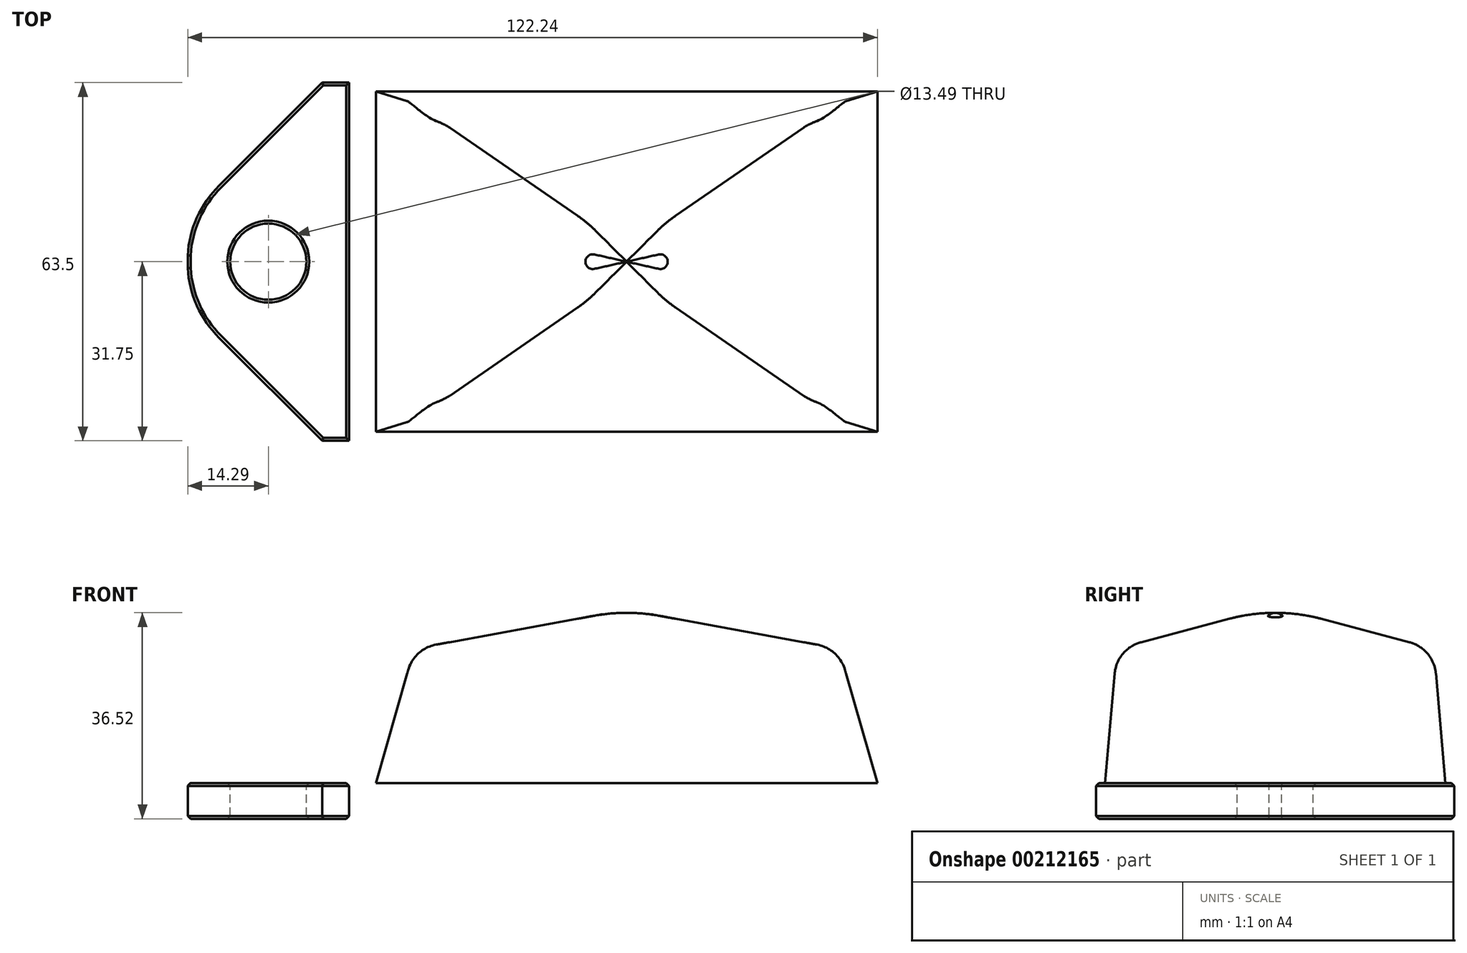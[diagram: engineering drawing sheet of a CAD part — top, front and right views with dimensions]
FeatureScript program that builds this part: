
annotation { "Feature Type Name" : "Feature", "Feature Type Description" : "" }
export const myFeature = defineFeature(function(context is Context, id is Id, definition is map)
    precondition{}
    {
        {
            var Q0;
            Q0=qCreatedBy(makeId("Right.planeOp"),FACE);
            var sketch = newSketch(context, id + "F0", { "sketchPlane" : qUnion([Q0])});
            skLineSegment(sketch, "E0.bottom", {"start": v(-31.75, 3.17) * mm, "end": v(31.75, 3.17) * mm});
            skLineSegment(sketch, "E0.top", {"start": v(-31.75, -3.17) * mm, "end": v(31.75, -3.17) * mm});
            skLineSegment(sketch, "E0.left", {"start": v(-31.75, 3.17) * mm, "end": v(-31.75, -3.17) * mm});
            skLineSegment(sketch, "E0.right", {"start": v(31.75, 3.17) * mm, "end": v(31.75, -3.17) * mm});
            skPoint(sketch, "E0.middle", {"position": v(0, 0) * mm});
            skLineSegment(sketch, "E1", {"start": v(0, 3.17) * mm, "end": v(0, 33.34) * mm, "construction": true});
            skPoint(sketch, "E1.endSnap0", {"position": v(0, 3.17) * mm});
            skLineSegment(sketch, "E2", {"start": v(0, 0) * mm, "end": v(30.16, 0) * mm, "construction": true});
            skLineSegment(sketch, "E3", {"start": v(0, 0) * mm, "end": v(-30.16, 0) * mm, "construction": true});
            skLineSegment(sketch, "E4", {"start": v(30.16, 0) * mm, "end": v(30.16, 3.17) * mm, "construction": true});
            skLineSegment(sketch, "E5", {"start": v(-30.16, 0) * mm, "end": v(-30.16, 3.17) * mm, "construction": true});
            skLineSegment(sketch, "E6", {"start": v(0, 26.99) * mm, "end": v(-32.25, 26.99) * mm, "construction": true});
            skLineSegment(sketch, "E7", {"start": v(30.16, 3.17) * mm, "end": v(28.47, 22.55) * mm});
            skLineSegment(sketch, "E8", {"start": v(0, 26.99) * mm, "end": v(37.6, 26.99) * mm, "construction": true});
            skPoint(sketch, "E9.visualSharp", {"position": v(0, 33.34) * mm});
            skPoint(sketch, "E10", {"position": v(0, 1.59) * mm});
            skLineSegment(sketch, "E11", {"start": v(23.77, 28.13) * mm, "end": v(8.14, 32.28) * mm});
            skPoint(sketch, "E12.visualSharp", {"position": v(28.08, 26.99) * mm});
            skLineSegment(sketch, "E13.MirrorCS", {"start": v(-23.77, 28.13) * mm, "end": v(-8.14, 32.28) * mm});
            skLineSegment(sketch, "E14.MirrorCS", {"start": v(-30.16, 3.17) * mm, "end": v(-28.47, 22.55) * mm});
            skArc(sketch, "E15", {"start": v(8.14, 32.28) * mm, "mid": v(0, 33.34) * mm, "end": v(-8.14, 32.28) * mm});
            skLineSegment(sketch, "E16", {"start": v(30.16, 3.17) * mm, "end": v(67.45, 3.17) * mm});
            skLineSegment(sketch, "E17", {"start": v(67.45, 3.17) * mm, "end": v(67.45, 46.58) * mm});
            skLineSegment(sketch, "E18", {"start": v(67.45, 46.58) * mm, "end": v(-44.32, 46.58) * mm});
            skLineSegment(sketch, "E19", {"start": v(-44.32, 46.58) * mm, "end": v(-44.32, 3.17) * mm});
            skLineSegment(sketch, "E20", {"start": v(-44.32, 3.17) * mm, "end": v(-31.75, 3.17) * mm});
            skLineSegment(sketch, "E21", {"start": v(-44.32, 3.17) * mm, "end": v(-44.32, -48.14) * mm});
            skLineSegment(sketch, "E22", {"start": v(-44.32, -48.14) * mm, "end": v(67.45, -48.14) * mm});
            skLineSegment(sketch, "E23", {"start": v(67.45, -48.14) * mm, "end": v(67.45, 3.17) * mm});
            skLineSegment(sketch, "E24", {"start": v(23.77, 28.13) * mm, "end": v(28.08, 26.99) * mm});
            skLineSegment(sketch, "E25", {"start": v(28.47, 22.55) * mm, "end": v(28.08, 26.99) * mm});
            skLineSegment(sketch, "E26.MirrorCS", {"start": v(-23.77, 28.13) * mm, "end": v(-28.08, 26.99) * mm});
            skLineSegment(sketch, "E27.MirrorCS", {"start": v(-28.47, 22.55) * mm, "end": v(-28.08, 26.99) * mm});
            skSolve(sketch);
        }
        {
            var Q0;
            Q0=makeQuery(id+"F0.imprint","IMPRINT",FACE,{"disambiguationData":[TD([[makeQuery(id+"F0.imprint","IMPRINT",EDGE,{"derivedFrom":sQuery(id+"F0.wireOp",EDGE,"E0.top")}),1.0]])]});
            extrude(context, id + "F1", {"entities" : qUnion([Q0]), "endBound" : BoundingType.SYMMETRIC, "depth" : 155.57 * mm});
        }
        {
            var Q0;
            Q0=qCreatedBy(makeId("Right.planeOp"),FACE);
            var sketch = newSketch(context, id + "F2", { "sketchPlane" : qUnion([Q0])});
            skLineSegment(sketch, "E28", {"start": v(0, 0) * mm, "end": v(0, 33.34) * mm, "construction": true});
            skLineSegment(sketch, "E29", {"start": v(0, 33.34) * mm, "end": v(0, -33.34) * mm});
            skArc(sketch, "E30", {"start": v(0, -33.34) * mm, "mid": v(33.34, 0) * mm, "end": v(0, 33.34) * mm});
            skSolve(sketch);
        }
        {
            var Q0;
            Q0=qCreatedBy(makeId("Front.planeOp"),FACE);
            var sketch = newSketch(context, id + "F3", { "sketchPlane" : qUnion([Q0])});
            skLineSegment(sketch, "E31", {"start": v(0, 0) * mm, "end": v(0, 33.34) * mm, "construction": true});
            skLineSegment(sketch, "E32", {"start": v(0, 3.18) * mm, "end": v(-44.45, 3.17) * mm, "construction": true});
            skLineSegment(sketch, "E33", {"start": v(-44.45, 3.17) * mm, "end": v(-38.7, 23.2) * mm});
            skLineSegment(sketch, "E34", {"start": v(-44.45, 3.17) * mm, "end": v(-44.45, 26.99) * mm});
            skLineSegment(sketch, "E35", {"start": v(-44.45, 26.99) * mm, "end": v(-37.62, 26.99) * mm, "construction": true});
            skLineSegment(sketch, "E36", {"start": v(0, 33.34) * mm, "end": v(-44.45, 33.34) * mm});
            skLineSegment(sketch, "E37", {"start": v(-44.45, 33.34) * mm, "end": v(-44.45, 26.99) * mm});
            skLineSegment(sketch, "E38.MirrorCS", {"start": v(44.45, 3.17) * mm, "end": v(38.96, 22.33) * mm});
            skLineSegment(sketch, "E39.MirrorCS", {"start": v(44.45, 3.17) * mm, "end": v(44.45, 26.99) * mm});
            skLineSegment(sketch, "E40.MirrorCS", {"start": v(44.45, 33.34) * mm, "end": v(44.45, 26.99) * mm});
            skLineSegment(sketch, "E41.MirrorCS", {"start": v(0, 33.34) * mm, "end": v(44.45, 33.34) * mm});
            skPoint(sketch, "E42.visualSharp", {"position": v(0, 33.34) * mm});
            skPoint(sketch, "E43", {"position": v(0, 1.59) * mm});
            skLineSegment(sketch, "E44", {"start": v(0, 1.59) * mm, "end": v(31.18, 32.77) * mm, "construction": true});
            skLineSegment(sketch, "E45.MirrorCS", {"start": v(0, 1.59) * mm, "end": v(-31.18, 32.77) * mm, "construction": true});
            skLineSegment(sketch, "E46.0", {"start": v(15.88, 0) * mm, "end": v(15.88, 30.3) * mm, "construction": true});
            skLineSegment(sketch, "E47.0", {"start": v(-15.88, 0) * mm, "end": v(-15.88, 30.3) * mm, "construction": true});
            skPoint(sketch, "E48.orphan", {"position": v(-38.96, 22.33) * mm});
            skLineSegment(sketch, "E49", {"start": v(-33.75, 27.7) * mm, "end": v(-5.7, 32.82) * mm});
            skLineSegment(sketch, "E50.MirrorCS", {"start": v(44.45, 3.17) * mm, "end": v(38.7, 23.2) * mm});
            skLineSegment(sketch, "E51.MirrorCS", {"start": v(33.75, 27.7) * mm, "end": v(5.7, 32.82) * mm});
            skPoint(sketch, "E52.visualSharp", {"position": v(-37.62, 26.99) * mm});
            skPoint(sketch, "E53.visualSharp", {"position": v(37.62, 26.99) * mm});
            skArc(sketch, "E54", {"start": v(5.7, 32.82) * mm, "mid": v(0, 33.34) * mm, "end": v(-5.7, 32.82) * mm});
            skLineSegment(sketch, "E55", {"start": v(44.45, 3.17) * mm, "end": v(-44.45, 3.17) * mm});
            skLineSegment(sketch, "E56", {"start": v(38.7, 23.2) * mm, "end": v(37.62, 26.99) * mm});
            skLineSegment(sketch, "E57", {"start": v(33.75, 27.7) * mm, "end": v(37.62, 26.99) * mm});
            skLineSegment(sketch, "E58", {"start": v(-33.75, 27.7) * mm, "end": v(-37.62, 26.99) * mm});
            skLineSegment(sketch, "E59", {"start": v(-38.7, 23.2) * mm, "end": v(-37.62, 26.99) * mm});
            skSolve(sketch);
        }
        {
            var Q0;
            Q0=qCreatedBy(makeId("Top.planeOp"),FACE);
            var sketch = newSketch(context, id + "F4", { "sketchPlane" : qUnion([Q0])});
            skLineSegment(sketch, "E60", {"start": v(0, 0) * mm, "end": v(-63.5, 0) * mm, "construction": true});
            skLineSegment(sketch, "E61.MirrorCS", {"start": v(0, 0) * mm, "end": v(63.5, 0) * mm, "construction": true});
            skCircle(sketch, "E62", {"center": v(-63.5, 0) * mm, "radius": 6.75 * mm});
            skCircle(sketch, "E63.MirrorC", {"center": v(63.5, 0) * mm, "radius": 6.75 * mm});
            skLineSegment(sketch, "E64", {"start": v(0, 0) * mm, "end": v(-85.72, 0) * mm, "construction": true});
            skLineSegment(sketch, "E65", {"start": v(-72.23, -13.5) * mm, "end": v(-53.98, -31.75) * mm});
            skLineSegment(sketch, "E66.MirrorCS", {"start": v(-72.23, 13.5) * mm, "end": v(-53.98, 31.75) * mm});
            skLineSegment(sketch, "E67", {"start": v(0, 0) * mm, "end": v(0, -31.75) * mm, "construction": true});
            skLineSegment(sketch, "E68", {"start": v(0, -31.75) * mm, "end": v(-53.98, -31.75) * mm});
            skPoint(sketch, "E69.orphan", {"position": v(-45.67, -40.06) * mm});
            skLineSegment(sketch, "E70.MirrorCS", {"start": v(0, 31.75) * mm, "end": v(-53.98, 31.75) * mm});
            skLineSegment(sketch, "E71.MirrorCS", {"start": v(0, 0) * mm, "end": v(0, 31.75) * mm, "construction": true});
            skPoint(sketch, "E72.orphan", {"position": v(-45.67, 40.06) * mm});
            skPoint(sketch, "E73", {"position": v(-58.74, 0) * mm});
            skLineSegment(sketch, "E74", {"start": v(-58.74, 0) * mm, "end": v(-72.23, 13.5) * mm, "construction": true});
            skLineSegment(sketch, "E75.MirrorCS", {"start": v(-58.74, 0) * mm, "end": v(-72.23, -13.5) * mm, "construction": true});
            skLineSegment(sketch, "E76", {"start": v(-85.72, 0) * mm, "end": v(-85.72, -31.75) * mm});
            skLineSegment(sketch, "E77", {"start": v(-85.72, -31.75) * mm, "end": v(-53.98, -31.75) * mm});
            skLineSegment(sketch, "E78", {"start": v(-85.73, 0) * mm, "end": v(-85.73, 31.75) * mm});
            skLineSegment(sketch, "E79", {"start": v(-85.73, 31.75) * mm, "end": v(-53.98, 31.75) * mm});
            skArc(sketch, "E80.MirrorCS", {"start": v(72.23, 13.5) * mm, "mid": v(77.82, 0) * mm, "end": v(72.23, -13.5) * mm});
            skLineSegment(sketch, "E81.MirrorCS", {"start": v(85.73, 0) * mm, "end": v(53.98, 31.75) * mm});
            skLineSegment(sketch, "E82.MirrorCS", {"start": v(85.73, 31.75) * mm, "end": v(53.98, 31.75) * mm});
            skLineSegment(sketch, "E83.MirrorCS", {"start": v(85.73, 0) * mm, "end": v(85.73, 31.75) * mm});
            skLineSegment(sketch, "E84.MirrorCS", {"start": v(85.72, 0) * mm, "end": v(85.72, -31.75) * mm});
            skLineSegment(sketch, "E85.MirrorCS", {"start": v(85.72, -31.75) * mm, "end": v(53.98, -31.75) * mm});
            skLineSegment(sketch, "E86.MirrorCS", {"start": v(85.73, 0) * mm, "end": v(53.98, -31.75) * mm});
            skArc(sketch, "E87", {"start": v(-72.23, -13.5) * mm, "mid": v(-77.82, 0) * mm, "end": v(-72.23, 13.5) * mm});
            skPoint(sketch, "E88.orphan", {"position": v(-85.73, 0) * mm});
            skSolve(sketch);
        }
        {
            var Q0;
            Q0=makeQuery(id+"F3.imprint","IMPRINT",FACE,{"disambiguationData":[TD([[makeQuery(id+"F3.imprint","IMPRINT",EDGE,{"derivedFrom":sQuery(id+"F3.wireOp",EDGE,"E33")}),-1.0]])]});
            extrude(context, id + "F5", {"entities" : qUnion([Q0]), "endBound" : BoundingType.SYMMETRIC, "depth" : 60.32 * mm});
        }
        {
            var Q0;
            {var subQ0=sQuery(id+"F0.wireOp",EDGE,"E7");Q0=makeQuery(id+"F0.imprint","IMPRINT",FACE,{"disambiguationData":[TD([[makeQuery(id+"F0.imprint","IMPRINT",EDGE,{"derivedFrom":subQ0}),1.0]])]});}
            extrude(context, id + "F6", {"entities" : qUnion([Q0]), "operationType" : NewBodyOperationType.ADD, "endBound" : BoundingType.SYMMETRIC, "depth" : 88.9 * mm});
        }
        {
            var Q0;
            {var subQ1=sQuery(id+"F3.wireOp",EDGE,"E39.MirrorCS");Q0=makeQuery(id+"F3.imprint","IMPRINT",FACE,{"disambiguationData":[TD([[makeQuery(id+"F3.imprint","IMPRINT",EDGE,{"derivedFrom":subQ1}),1.0]])]});}
            var Q1;
            Q1=makeQuery(id+"F3.imprint","IMPRINT",FACE,{"disambiguationData":[TD([[makeQuery(id+"F3.imprint","IMPRINT",EDGE,{"derivedFrom":sQuery(id+"F3.wireOp",EDGE,"E33")}),1.0]])]});
            extrude(context, id + "F7", {"entities" : qUnion([Q0, Q1]), "operationType" : NewBodyOperationType.REMOVE, "endBound" : BoundingType.SYMMETRIC, "oppositeDirection" : true, "depth" : 60.32 * mm});
        }
        {
            var Q0;
            {var subQ4=sQuery(id+"F0.wireOp",EDGE,"E7");Q0=makeQuery(id+"F0.imprint","IMPRINT",FACE,{"disambiguationData":[TD([[makeQuery(id+"F0.imprint","IMPRINT",EDGE,{"derivedFrom":subQ4}),-1.0]])]});}
            extrude(context, id + "F8", {"entities" : qUnion([Q0]), "operationType" : NewBodyOperationType.REMOVE, "endBound" : BoundingType.SYMMETRIC, "oppositeDirection" : true, "depth" : 88.9 * mm});
        }
        {
            var Q0;
            Q0=makeQuery(id+"F2.imprint","IMPRINT",FACE,{"disambiguationData":[TD([[makeQuery(id+"F2.imprint","IMPRINT",EDGE,{"derivedFrom":sQuery(id+"F2.wireOp",EDGE,"E29")}),1.0]])]});
            var Q1;
            Q1=sQuery(id+"F2.wireOp",EDGE,"E30");
            var Q2;
            Q2=sQuery(id+"F2.wireOp",EDGE,"E29");
            revolve(context, id + "F9", {"operationType" : NewBodyOperationType.ADD, "entities" : qUnion([Q0]), "surfaceEntities" : qUnion([Q1]), "axis" : qUnion([Q2]), "revolveType" : RevolveType.FULL});
        }
        {
            var Q0;
            Q0=makeQuery(id+"F1.opExtrude","CAP_FACE",FACE,{"disambiguationData":[OSD([sQuery(id+"F0.wireOp",EDGE,"E0.bottom"),sQuery(id+"F0.wireOp",EDGE,"E0.top"),sQuery(id+"F0.wireOp",EDGE,"E0.left"),sQuery(id+"F0.wireOp",EDGE,"E0.right"),sQuery(id+"F0.wireOp",EDGE,"E16")])],"isStart":false});
            var Q1;
            {var subQ4=sQuery(id+"F0.wireOp",EDGE,"E7");Q1=makeQuery(id+"F0.imprint","IMPRINT",FACE,{"disambiguationData":[TD([[makeQuery(id+"F0.imprint","IMPRINT",EDGE,{"derivedFrom":subQ4}),-1.0]])]});}
            var Q2;
            Q2=makeQuery(id+"F0.imprint","IMPRINT",FACE,{"disambiguationData":[TD([[makeQuery(id+"F0.imprint","IMPRINT",EDGE,{"derivedFrom":sQuery(id+"F0.wireOp",EDGE,"E0.top")}),-1.0]])]});
            extrude(context, id + "F10", {"entities" : qUnion([Q0, Q1, Q2]), "operationType" : NewBodyOperationType.REMOVE, "endBound" : BoundingType.SYMMETRIC, "oppositeDirection" : true, "depth" : 254 * mm});
        }
        {
            var Q0;
            Q0=makeQuery(id+"F8.boolean.opBoolean","COPY",EDGE,{"derivedFrom":makeQuery(id+"F8.opExtrude","SWEPT_EDGE",EDGE,{"disambiguationData":[OSD([sQuery(id+"F0.wireOp",EDGE,"E26.MirrorCS"),sQuery(id+"F0.wireOp",EDGE,"E27.MirrorCS")])]})});
            var Q1;
            {var subQ0=sQuery(id+"F3.wireOp",EDGE,"E57");var subQ1=sQuery(id+"F3.wireOp",EDGE,"E56");var subQ12=makeQuery(id+"F5.opExtrude","SWEPT_EDGE",EDGE,{"disambiguationData":[OSD([subQ1,subQ0])]});Q1=makeQuery(id+"F7.boolean.opBoolean","MERGE",EDGE,{"derivedFrom":[makeQuery(id+"F6.boolean.opBoolean","SPLIT",EDGE,{"disambiguationData":[TD([makeQuery(id+"F6.opExtrude","SWEPT_FACE",FACE,{"disambiguationData":[OSD([sQuery(id+"F0.wireOp",EDGE,"E7"),sQuery(id+"F0.wireOp",EDGE,"E25")])]})])],"derivedFrom":subQ12}),makeQuery(id+"F6.boolean.opBoolean","SPLIT",EDGE,{"disambiguationData":[TD([makeQuery(id+"F6.opExtrude","SWEPT_FACE",FACE,{"disambiguationData":[OSD([sQuery(id+"F0.wireOp",EDGE,"E13.MirrorCS"),sQuery(id+"F0.wireOp",EDGE,"E26.MirrorCS")])]})])],"derivedFrom":subQ12}),makeQuery(id+"F7.opExtrude","SWEPT_EDGE",EDGE,{"disambiguationData":[OSD([subQ1,subQ0])]})]});}
            var Q2;
            Q2=makeQuery(id+"F8.boolean.opBoolean","COPY",EDGE,{"derivedFrom":makeQuery(id+"F8.opExtrude","SWEPT_EDGE",EDGE,{"disambiguationData":[OSD([sQuery(id+"F0.wireOp",EDGE,"E24"),sQuery(id+"F0.wireOp",EDGE,"E25")])]})});
            var Q3;
            {var subQ0=sQuery(id+"F3.wireOp",EDGE,"E59");var subQ1=sQuery(id+"F3.wireOp",EDGE,"E58");var subQ12=makeQuery(id+"F5.opExtrude","SWEPT_EDGE",EDGE,{"disambiguationData":[OSD([subQ1,subQ0])]});Q3=makeQuery(id+"F7.boolean.opBoolean","MERGE",EDGE,{"derivedFrom":[makeQuery(id+"F6.boolean.opBoolean","SPLIT",EDGE,{"disambiguationData":[TD([makeQuery(id+"F6.opExtrude","SWEPT_FACE",FACE,{"disambiguationData":[OSD([sQuery(id+"F0.wireOp",EDGE,"E7"),sQuery(id+"F0.wireOp",EDGE,"E25")])]})])],"derivedFrom":subQ12}),makeQuery(id+"F6.boolean.opBoolean","SPLIT",EDGE,{"disambiguationData":[TD([makeQuery(id+"F6.opExtrude","SWEPT_FACE",FACE,{"disambiguationData":[OSD([sQuery(id+"F0.wireOp",EDGE,"E13.MirrorCS"),sQuery(id+"F0.wireOp",EDGE,"E26.MirrorCS")])]})])],"derivedFrom":subQ12}),makeQuery(id+"F7.opExtrude","SWEPT_EDGE",EDGE,{"disambiguationData":[OSD([subQ1,subQ0])]})]});}
            fillet(context, id + "F11", {"entities" : qUnion([Q0, Q1, Q2, Q3]), "radius" : 6.35 * mm, "tangentPropagation" : true, "allowEdgeOverflow" : false});
        }
        {
            var Q0;
            Q0=makeQuery(id+"F4.imprint","IMPRINT",FACE,{"disambiguationData":[TD([[makeQuery(id+"F4.imprint","IMPRINT",EDGE,{"derivedFrom":sQuery(id+"F4.wireOp",EDGE,"E65")}),-1.0]])]});
            var Q1;
            Q1=makeQuery(id+"F4.imprint","IMPRINT",FACE,{"disambiguationData":[TD([[makeQuery(id+"F4.imprint","IMPRINT",EDGE,{"derivedFrom":sQuery(id+"F4.wireOp",EDGE,"E62")}),1.0]])]});
            var Q2;
            Q2=makeQuery(id+"F4.imprint","IMPRINT",FACE,{"disambiguationData":[TD([[makeQuery(id+"F4.imprint","IMPRINT",EDGE,{"derivedFrom":sQuery(id+"F4.wireOp",EDGE,"E63.MirrorC")}),-1.0]])]});
            var Q3;
            {var subQ0=sQuery(id+"F4.wireOp",EDGE,"E80.MirrorCS");Q3=makeQuery(id+"F4.imprint","IMPRINT",FACE,{"disambiguationData":[TD([[makeQuery(id+"F4.imprint","IMPRINT",EDGE,{"derivedFrom":subQ0}),1.0]])]});}
            var Q4;
            {var subQ3=sQuery(id+"F4.wireOp",EDGE,"E82.MirrorCS");Q4=makeQuery(id+"F4.imprint","IMPRINT",FACE,{"disambiguationData":[TD([[makeQuery(id+"F4.imprint","IMPRINT",EDGE,{"derivedFrom":subQ3}),1.0]])]});}
            var Q5;
            {var subQ0=sQuery(id+"F4.wireOp",EDGE,"E84.MirrorCS");Q5=makeQuery(id+"F4.imprint","IMPRINT",FACE,{"disambiguationData":[TD([[makeQuery(id+"F4.imprint","IMPRINT",EDGE,{"derivedFrom":subQ0}),-1.0]])]});}
            extrude(context, id + "F12", {"entities" : qUnion([Q0, Q1, Q2, Q3, Q4, Q5]), "operationType" : NewBodyOperationType.REMOVE, "endBound" : BoundingType.SYMMETRIC, "oppositeDirection" : true, "depth" : 50.8 * mm});
        }
        {
            var Q0;
            Q0=makeQuery(id+"F1.opExtrude","SWEPT_FACE",FACE,{"disambiguationData":[OSD([sQuery(id+"F0.wireOp",EDGE,"E0.top")])]});
            var Q1;
            Q1=makeQuery(id+"F1.opExtrude","SWEPT_FACE",FACE,{"disambiguationData":[OSD([sQuery(id+"F0.wireOp",EDGE,"E0.bottom"),sQuery(id+"F0.wireOp",EDGE,"E16")])]});
            chamfer(context, id + "F13", {"entities" : qUnion([Q0, Q1]), "width" : 0.5 * mm, "tangentPropagation" : true});
        }
    });
